FCSTD DOCUMENT  (FreeCAD 0.21R33771 (Git))
Label: ВОРК
License: All rights reserved
LicenseURL: https://en.wikipedia.org/wiki/All_rights_reserved
objects: Sketcher::SketchObject×1, PartDesign::Body×1
note: 2 computed .brp shape members not serialized (recipe doc carries the construction recipe); baked Part::Feature solids carry a one-line shape summary decoded from their .brp

FEATURE [Sketcher::SketchObject] Sketch
  FullyConstrained = true
  MapMode = 5
  Support = -> [XY_Plane]
  sketch-geometry (21):
    g0: LineSegment StartX=11.15 StartY=-6.4 StartZ=0 EndX=11.15 EndY=6.4 EndZ=0
    g1: LineSegment StartX=11.15 StartY=6.4 StartZ=0 EndX=-11.15 EndY=6.4 EndZ=0
    g2: LineSegment StartX=-11.15 StartY=6.4 StartZ=0 EndX=-11.15 EndY=-6.4 EndZ=0
    g3: LineSegment StartX=-11.15 StartY=-6.4 StartZ=0 EndX=11.15 EndY=-6.4 EndZ=0
    g4: GeomPoint X=0 Y=0 Z=0
    g5: LineSegment StartX=14.1807 StartY=-6.4 StartZ=0 EndX=14.1807 EndY=6.4 EndZ=0
    g6: LineSegment StartX=11.1807 StartY=9.4 StartZ=0 EndX=-14.1807 EndY=9.4 EndZ=0
    g7: LineSegment StartX=-14.15 StartY=4.15 StartZ=0 EndX=-14.15 EndY=-5.35 EndZ=0
    g8: LineSegment StartX=-14.1193 StartY=-9.4 StartZ=0 EndX=11.1807 EndY=-9.4 EndZ=0
    g9: GeomPoint X=0 Y=0 Z=0
    g10: ArcOfCircle CenterX=-71.15 CenterY=0 CenterZ=0 NormalX=0 NormalY=0 NormalZ=1 AngleXU=0 Radius=3 StartAngle=1.80822 EndAngle=6.52899
    g11: ArcOfCircle CenterX=-17.3146 CenterY=-222.469 CenterZ=0 NormalX=0 NormalY=0 NormalZ=1 AngleXU=0 Radius=231.89 StartAngle=1.55728 EndAngle=1.80822
    g12: ArcOfCircle CenterX=-19.7474 CenterY=-197.744 CenterZ=0 NormalX=0 NormalY=0 NormalZ=1 AngleXU=0 Radius=204.32 StartAngle=1.55496 EndAngle=1.70198
    g13: ArcOfCircle CenterX=-55.9847 CenterY=-83.4324 CenterZ=0 NormalX=0 NormalY=0 NormalZ=1 AngleXU=0 Radius=85.05 StartAngle=1.05613 EndAngle=1.7154
    g14: ArcOfCircle CenterX=-53.3593 CenterY=-73.518 CenterZ=0 NormalX=0 NormalY=0 NormalZ=1 AngleXU=0 Radius=78.64 StartAngle=1.04882 EndAngle=1.48313
    g15: ArcOfCircle CenterX=-53.3593 CenterY=-73.518 CenterZ=0 NormalX=0 NormalY=0 NormalZ=1 AngleXU=0 Radius=78.64 StartAngle=1.80822 EndAngle=1.80822
    g16: ArcOfCircle CenterX=11.1807 CenterY=6.4 CenterZ=0 NormalX=0 NormalY=0 NormalZ=1 AngleXU=0 Radius=3 StartAngle=1e-16 EndAngle=1.5708
    g17: GeomPoint X=14.1807 Y=9.4 Z=0
    g18: ArcOfCircle CenterX=11.1807 CenterY=-6.4 CenterZ=0 NormalX=0 NormalY=0 NormalZ=1 AngleXU=0 Radius=3 StartAngle=4.71239 EndAngle=6.28319
    g19: GeomPoint X=14.1807 Y=-9.4 Z=0
    g20: ArcOfCircle CenterX=-16.5503 CenterY=4.15 CenterZ=0 NormalX=0 NormalY=0 NormalZ=1 AngleXU=0 Radius=2.4003 StartAngle=0 EndAngle=1.55496
  constraints (55):
    c: Coincident(g0,g1)
    c: Coincident(g1,g2)
    c: Coincident(g2,g3)
    c: Coincident(g3,g0)
    c: Horizontal(g1)
    c: Horizontal(g3)
    c: Vertical(g0)
    c: Vertical(g2)
    c: Symmetric(g1,g0,g4)
    c: Coincident(g4,g-1)
    c: DistanceX(g1,g1) = 22.3
    c: DistanceY(g0,g0) = 12.8
    c: Horizontal(g6)
    c: Horizontal(g8)
    c: Vertical(g5)
    c: Vertical(g7)
    c: Symmetric(g6,g19,g9)
    c: Coincident(g9,g4)
    c: DistanceY(g8,g6) = 18.8
    c: DistanceX(g8,g19) = 28.3
    c: PointOnObject(g10,g-1)
    c: Radius(g10) = 3
    c: DistanceX(g10,g2) = 60
    c: Coincident(g11,g6)
    c: Radius(g11) = 231.89
    c: Radius(g12) = 204.32
    c: Tangent(g10,g11) = -1.5708
    c: DistanceY(g-1,g10) = 0.73
    c: Coincident(g13,g10)
    c: Coincident(g13,g8)
    c: Radius(g13) = 85.05
    c: Coincident(g15,g10)
    c: Radius(g14) = 78.64
    c: Coincident(g7,g14)
    c: DistanceY(g7,g-1) = 5.35
    c: Equal(g14,g15)
    c: Tangent(g15,g11) = -1.5708
    c: Coincident(g14,g15)
    c: Coincident(g12,g14)
    c: DistanceY(g-1,g12) = 4.82
    c: PointOnObject(g17,g5)
    c: PointOnObject(g17,g6)
    c: Tangent(g5,g16) = -1.5708
    c: Tangent(g6,g16) = -1.5708
    c: PointOnObject(g19,g8)
    c: PointOnObject(g19,g5)
    c: Tangent(g8,g18) = -1.5708
    c: Tangent(g5,g18) = -1.5708
    c: Radius(g18) = 3
    c: Radius(g16) = 3
    c: Tangent(g7,g20) = 1.5708
    c: Tangent(g12,g20) = -1.5708
    c: DistanceX(g7,g-1) = 14.15
    c: DistanceY(g-1,g7) = 4.15
    c: DistanceY(g-1,g12) = 6.55
FEATURE [PartDesign::Body] Body
  Group = -> [Sketch]
  Origin = -> Origin
